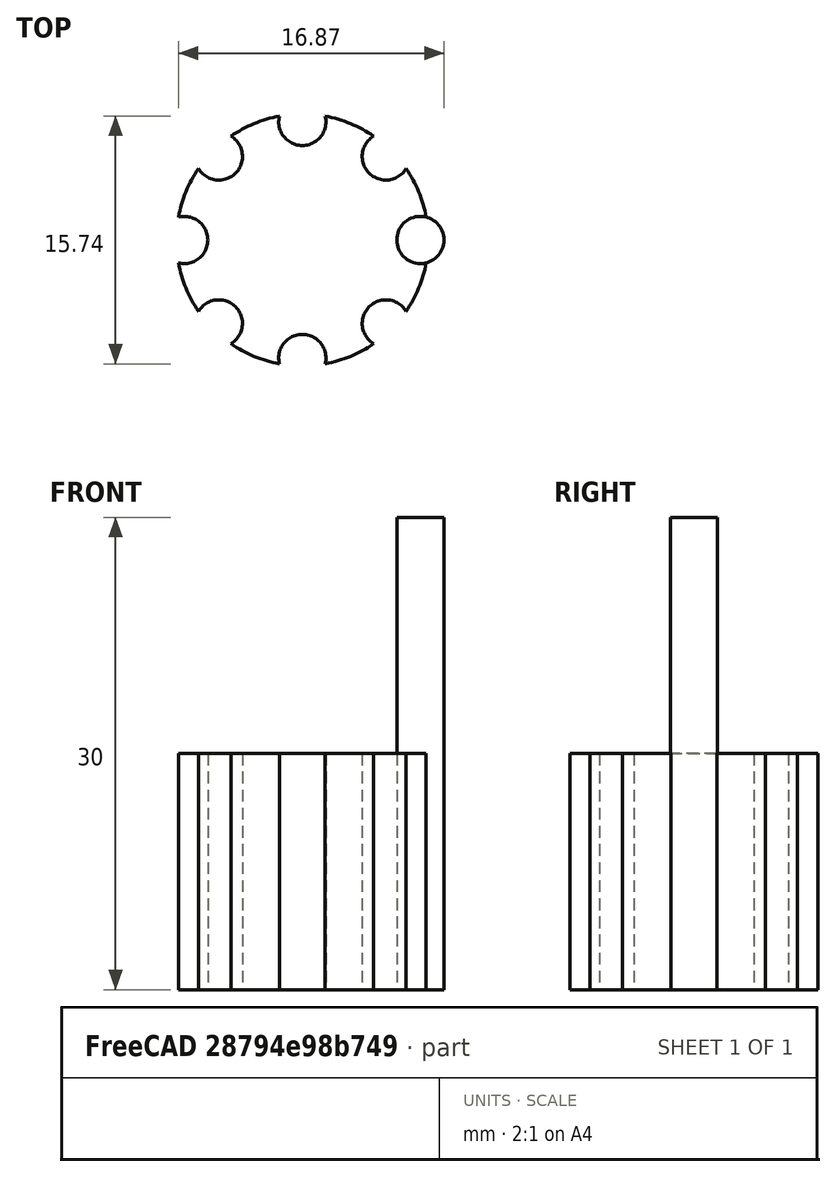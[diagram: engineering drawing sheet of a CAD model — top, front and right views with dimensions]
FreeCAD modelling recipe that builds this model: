
FCSTD DOCUMENT  (FreeCAD 1.0R39319 (Git))
Label: ojt1_t11r01_buttom
License: All rights reserved
LicenseURL: https://en.wikipedia.org/wiki/All_rights_reserved
objects: Part::Cylinder×2, Part::FeaturePython×1, Part::Cut×1
note: 3 computed .brp shape members not serialized (recipe doc carries the construction recipe); baked Part::Feature solids carry a one-line shape summary decoded from their .brp

FEATURE [Part::Cylinder] Cylinder  label="Cilindre"
  Angle = 360
  AttacherType = Attacher::AttachEngine3D
  FirstAngle = 0
  Height = 15
  Radius = 8
  SecondAngle = 0
FEATURE [Part::Cylinder] Cylinder001  label="Cilindre001"
  Angle = 360
  AttacherType = Attacher::AttachEngine3D
  FirstAngle = 0
  Height = 30
  Placement = pos=(7.5,0,0) rot=(0,0,1;0rad)
  Radius = 1.5
  SecondAngle = 0
FEATURE [Part::FeaturePython] Array  # Draft array (typed FeaturePython)
  AlwaysSyncPlacement = false
  Angle = 360
  ArrayType = 1
  Axis = (0,0,1)
  Base = -> Cylinder001
  Center = (0,0,0)
  Count = 8
  ExpandArray = false
  Fuse = false
  IntervalAxis = (0,0,0)
  IntervalX = (50,0,0)
  IntervalY = (0,50,0)
  IntervalZ = (0,0,50)
  NumberCircles = 3
  NumberPolar = 8
  NumberX = 2
  NumberY = 2
  NumberZ = 1
  PlacementList = 8 placements: [(7.5,0,0),(5.3033,5.3033,0),(0,7.5,0),(-5.3033,5.3033,0),(-7.5,9.18485e-16,0),(-5.3033,-5.3033,0),(-1.66533e-15,-7.5,0),(5.3033,-5.3033,0)]
  RadialDistance = 50
  ScaleList = (8) [(1,1,1),(1,1,1),(1,1,1),(1,1,1),(1,1,1),(1,1,1),(1,1,1),(1,1,1)]
  Symmetry = 1
  TangentialDistance = 25
FEATURE [Part::Cut] Cut
  Base = -> Cylinder
  Refine = true
  Tool = -> Array
